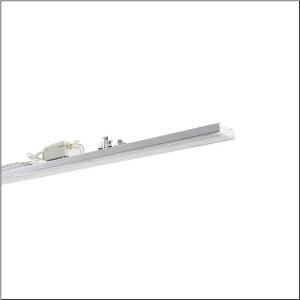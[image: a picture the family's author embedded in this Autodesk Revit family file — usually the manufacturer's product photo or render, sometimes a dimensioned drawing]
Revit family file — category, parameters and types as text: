
# Revit family: licross_r__21_recessed_mo_52tl147n48xg_d69c
name_source: partatom
category: Lighting Fixtures
units: mm (PartAtom-declared; Revit-internal decimal feet)

## family parameters
Cut with Voids When Loaded = No
Host = Face
Light Source = No
Part Type = Normal
Room Calculation Point = No
Round Connector Dimension = Use Diameter
Shared = No

## types (1)
- Licross® 21 Recessed MO (1 x LED, 8120 lm, 47.9 W, 4000K)
    Apparent Load = 48 VA
    CIE Flux Codes = 56 84 97 100 100
    Color Rendering = 80
    Color Temperature = 4000K
    Default Elevation = 1800 mm
    Description = Licross® 21 Recessed MO, luminaire insert, of sheet steel, galvanised, coil coated, white, length: 1.500mm, width: 66mm, height: 67mm, LED rated luminous flux: 8.120lm, light colour: 840, control gear: ON/OFF, with plug, 3-pole, with phase selection, mains connection: 220..240V, AC, 50/60Hz, rated input power: 48W, halogen-free wiring, primary light control with lens, of plastic, primary optical cover: cover, of PMMA, light emission: direct distribution, primary light characteristic: asymmetric, protection rating (complete): IP40, insulation class (complete): insulation class I (protective earthing), certification: CE, ENEC, VDE, UKCA, protection symbol: D if used in an environment without relevant dust loads with corresponding accessories, impact resistance: IK06, permissible ambient temperature for indoor applications: -35..+40°C, corresponds to IFS (International Featured Standards) requirements for safety and quality in the food industry, reducing of maximum allowable ambient temperature of 5°C with ceiling mounting, LABS conformity tested according to VDMA 24364:2018-05, packaging unit: 1 piece
    Height = 58 mm
    Lamp = 1 x LED
    Lamp Light Flux = 8120 lm
    Lamp Power = 47.9 W
    Lamp count = 1
    Length = 1500 mm
    Luminous efficacy = 170 lm/W
    Manufacturer = Siteco
    ModVariant = No
    Model = 52TL147N48XG
    Mounting Place = Ceiling
    Mounting Type = Pendant
    Number of Poles = 1
    OnlyDefault = Yes
    Power Factor = 1
    Product Name = Licross® 21 Recessed MO
    Product group = luminaire insert
    ProductGroupID = 901
    Protection Class = Protection class I
    Protection Degree = IP 40
    RLX_Detail_Level = 1
    RLX_Emergency_Light_Flux = 0 lm
    RLX_Emergency_Type = 0
    RLX_Emergency_Type_DB = No
    RlxData = <blob elided: 21345 chars, md5=8e06be8c>
    Socket = socket
    Standby Power = 0 W
    System Light Flux = 8120 lm
    System Power = 48 W
    Type Comments = Product without accessories
    Type Image = l_1296930.jpg
    URL = http://relux.com
    VarID = ---
    Voltage = 0 V
    Weight = 0.00 kg
    Width = 66 mm

## geometry (parser evidence)
native form markers: Blend x4, Sweep x10
no freeform markers — native parametric forms only
